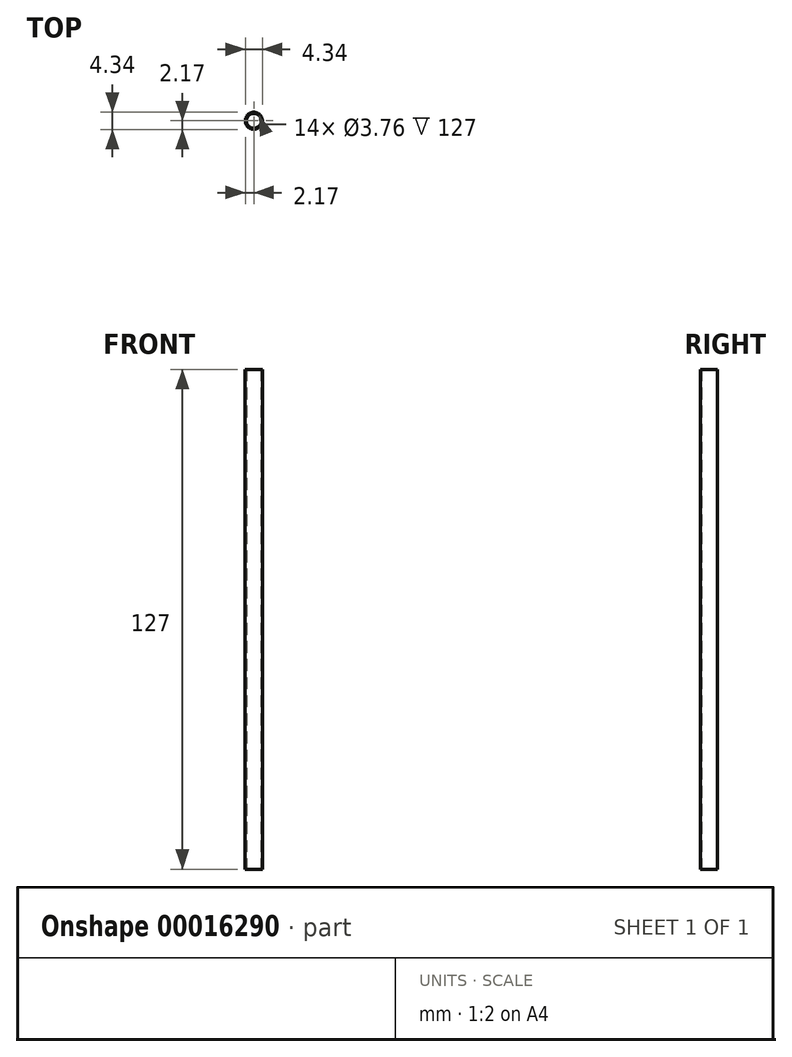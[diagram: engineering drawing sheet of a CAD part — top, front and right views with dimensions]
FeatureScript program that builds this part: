
annotation { "Feature Type Name" : "Feature", "Feature Type Description" : "" }
export const myFeature = defineFeature(function(context is Context, id is Id, definition is map)
    precondition{}
    {
        {
            var Q0;
            Q0=qCreatedBy(makeId("Front.planeOp"),FACE);
            var sketch = newSketch(context, id + "F0", { "sketchPlane" : qUnion([Q0])});
            skLineSegment(sketch, "E0", {"start": v(0, 0) * mm, "end": v(1.88, 0) * mm});
            skLineSegment(sketch, "E1", {"start": v(1.88, 0) * mm, "end": v(1.88, 127) * mm});
            skLineSegment(sketch, "E2", {"start": v(1.88, 127) * mm, "end": v(2.17, 127) * mm});
            skLineSegment(sketch, "E3", {"start": v(2.17, 127) * mm, "end": v(2.17, 0) * mm});
            skLineSegment(sketch, "E4", {"start": v(2.17, 0) * mm, "end": v(1.88, 0) * mm});
            skLineSegment(sketch, "E5", {"start": v(0, 0) * mm, "end": v(0, 127) * mm});
            skLineSegment(sketch, "E6", {"start": v(0, 127) * mm, "end": v(1.88, 127) * mm});
            skSolve(sketch);
        }
        {
            var Q0;
            Q0=makeQuery(id+"F0.imprint","IMPRINT",FACE,{"disambiguationData":[TD([[makeQuery(id+"F0.imprint","IMPRINT",EDGE,{"derivedFrom":sQuery(id+"F0.wireOp",EDGE,"E1")}),-1.0]])]});
            var Q1;
            Q1=sQuery(id+"F0.wireOp",EDGE,"E5");
            revolve(context, id + "F1", {"entities" : qUnion([Q0]), "axis" : qUnion([Q1]), "revolveType" : RevolveType.FULL});
        }
    });
